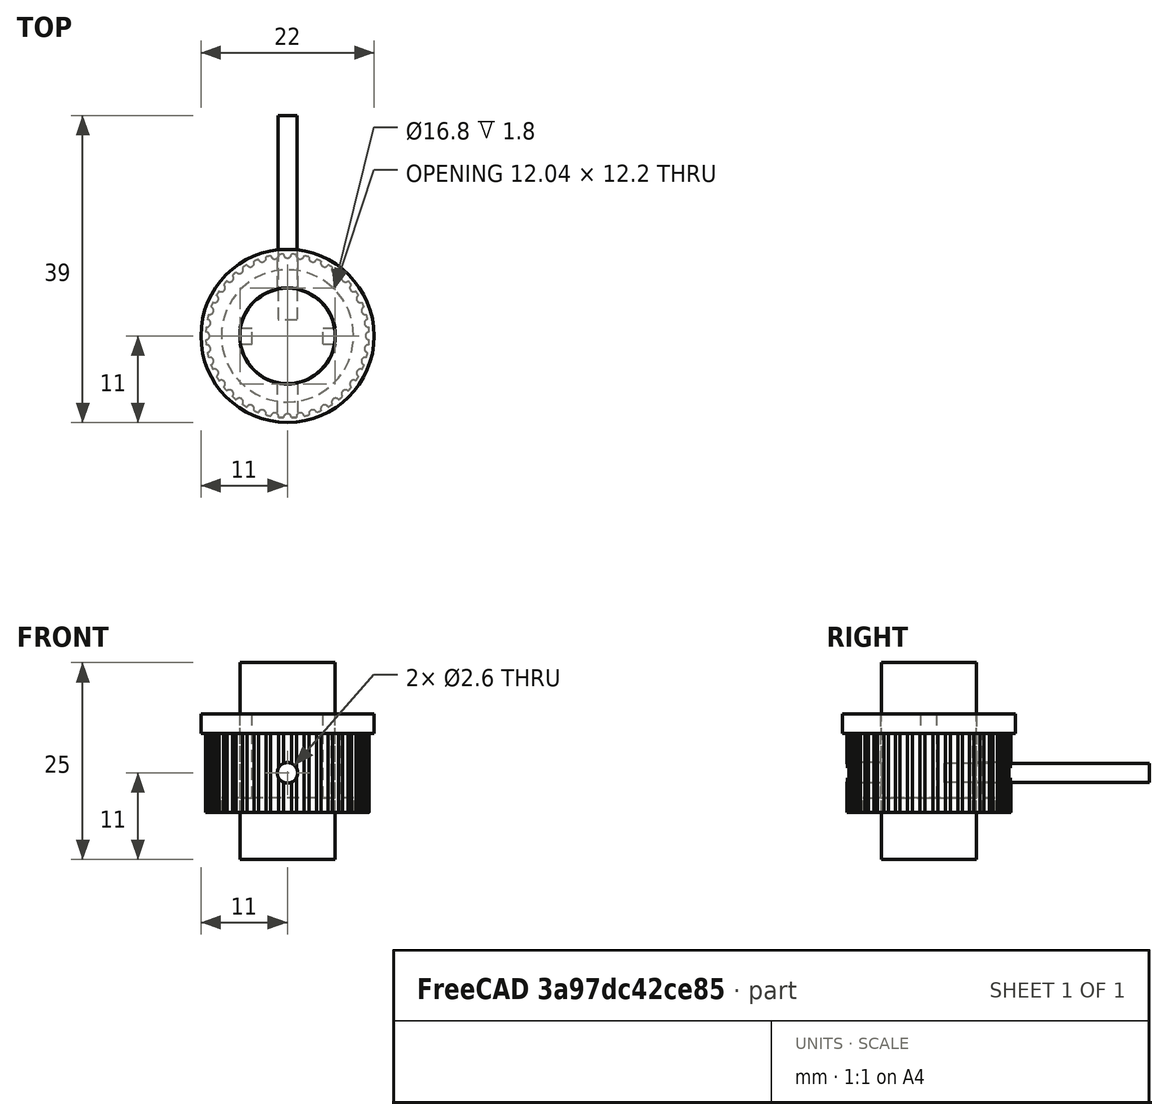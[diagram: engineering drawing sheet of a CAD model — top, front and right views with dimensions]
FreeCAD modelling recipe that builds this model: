
FCSTD DOCUMENT  (FreeCAD 0.17R13522 (Git))
Label: v5_perilla2_grande
License: CreativeCommons Attribution-ShareAlike
LicenseURL: http://creativecommons.org/licenses/by-sa/4.0/
objects: Part::Cut×8, Part::Cylinder×7, Part::Feature×4, Part::Fuse×2, Part::Box×2, Part::FeaturePython×1
note: 24 computed .brp shape members not serialized (recipe doc carries the construction recipe); baked Part::Feature solids carry a one-line shape summary decoded from their .brp

FEATURE [Part::Cylinder] Cylinder
  Angle = 360
  AttacherType = Attacher::AttachEngine3D
  Height = 2.5
  Radius = 11
FEATURE [Part::Cylinder] Cylinder001  label="agujereador del medio"
  Angle = 360
  AttacherType = Attacher::AttachEngine3D
  Height = 25
  Placement = pos=(0,0,-16) rot=(0,0,1;0rad)
  Radius = 6.1
FEATURE [Part::Cut] Cut
  Base = -> Cylinder
  Refine = true
  Tool = -> Cylinder001
FEATURE [Part::Cylinder] Cylinder002
  Angle = 360
  AttacherType = Attacher::AttachEngine3D
  Height = 12.2
  Placement = pos=(0,0,-10) rot=(0,0,1;0rad)
  Radius = 10.4
FEATURE [Part::Feature] Cylinder001001  label="Cylinder003"
  Placement = pos=(0,0,-16) rot=(0,0,1;0rad)
  shape: bbox 12.1 x 12.1 x 25 mm, 3 faces (baked)
FEATURE [Part::Feature] Cylinder001002  label="Cylinder004"
  Placement = pos=(0,0,-16) rot=(0,0,1;0rad)
  shape: bbox 12.1 x 12.1 x 25 mm, 3 faces (baked)
FEATURE [Part::Cylinder] Cylinder001003  label="Cylinder005"
  Angle = 360
  AttacherType = Attacher::AttachEngine3D
  Height = 10
  Placement = pos=(0,0,-18.2) rot=(0,0,1;0rad)
  Radius = 8.4
FEATURE [Part::Fuse] Fusion
  Base = -> Cut
  Refine = true
  Tool = -> Cylinder002
FEATURE [Part::Cut] Cut001
  Base = -> Fusion
  Refine = true
  Tool = -> Cylinder001003
FEATURE [Part::Cut] Cut002
  Base = -> Cut001
  Refine = true
  Tool = -> Cylinder001
FEATURE [Part::Cylinder] Cylinder001004  label="cavador_base"
  Angle = 360
  AttacherType = Attacher::AttachEngine3D
  Height = 12
  Placement = pos=(-10.4,0,-12) rot=(0,0,1;0rad)
  Radius = 0.5
FEATURE [Part::FeaturePython] Array  # Draft array (typed FeaturePython)
  Angle = 360
  ArrayType = 1
  Axis = (0,0,1)
  Base = -> Cylinder001004
  Center = (0,0,0)
  Fuse = false
  IntervalAxis = (0,0,0)
  IntervalX = (1,0,0)
  IntervalY = (0,1,0)
  IntervalZ = (0,0,0)
  NumberPolar = 40
  NumberX = 0
  NumberY = 0
  NumberZ = 0
FEATURE [Part::Cut] Cut003  label="el boton sin agujero"
  Base = -> Cut002
  Refine = true
  Tool = -> Array
FEATURE [Part::Cylinder] Cylinder001005  label="barilla perfora alen"
  Angle = 360
  AttacherType = Attacher::AttachEngine3D
  Height = 26
  Placement = pos=(0,0,-5) rot=(1,0,0;1.5708rad)
  Radius = 1.2
FEATURE [Part::Feature] Cylinder001005001  label="barilla perfora alen001"
  Placement = pos=(0,28,-5) rot=(1,0,0;1.5708rad)
  shape: bbox 2.4 x 26 x 2.4 mm, 3 faces (baked)
FEATURE [Part::Cut] Cut004  label="perilla con un agujero para allen"
  Base = -> Cut003
  Refine = true
  Tool = -> Cylinder001005
FEATURE [Part::Cylinder] Cylinder001005002  label="barilla perfora alen 2.6 mm"
  Angle = 360
  AttacherType = Attacher::AttachEngine3D
  Height = 18
  Placement = pos=(0,0,-5) rot=(1,0,0;1.5708rad)
  Radius = 1.3
FEATURE [Part::Cut] Cut005  label="perilla grande"
  Base = -> Cut004
  Refine = true
  Tool = -> Cylinder001005002
FEATURE [Part::Box] Box  label="aleta grande entera"
  AttacherType = Attacher::AttachEngine3D
  Height = 10.7
  Length = 14
  Placement = pos=(-7,-1,-8.2) rot=(0,0,1;0rad)
  Width = 2
FEATURE [Part::Box] Box001  label="cortador aleta grande"
  AttacherType = Attacher::AttachEngine3D
  Height = 10.7
  Length = 9
  Placement = pos=(-4.5,-1,-8.2) rot=(0,0,1;0rad)
  Width = 2
FEATURE [Part::Fuse] Fusion001
  Base = -> Cut005
  Refine = true
  Tool = -> Box
FEATURE [Part::Cut] Cut006  label="perilla grande con aletas"
  Base = -> Fusion001
  Refine = true
  Tool = -> Box001
FEATURE [Part::Feature] Cylinder001005002001  label="barilla perfora alen 2.6 mm001"
  Placement = pos=(0,21,-5) rot=(1,0,0;1.5708rad)
  shape: bbox 2.6 x 18 x 2.6 mm, 3 faces (baked)
FEATURE [Part::Cut] Cut007  label="perilla grande con 2 agujeros allen y aletas"
  Base = -> Cut006
  Refine = true
  Tool = -> Cylinder001005002001
